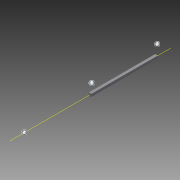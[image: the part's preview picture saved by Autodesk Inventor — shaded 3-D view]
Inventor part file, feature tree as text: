
AUTODESK INVENTOR PART (.ipt)
format: ipt  version: 2015 (Build 190159000, 159)  size: 156,672 bytes
history: native  units: in
note: dims shown in document units (in); Inventor stores cm internally (conversion verified against a paired STEP export)
features: other x5, extrude x1, imported_body x1, sketch x1
ambient origin geometry x8: Origin, YZ Plane, XZ Plane, XY Plane, X Axis, Y Axis, Z Axis, Center Point
bodies: Body1 (feature_tree)
feature tree (8):
  parser-record x1  (decoder bookkeeping rows leaked as tree rows — omitted from the tree; the rows remain in map.json)
  other  "Shaft"
  extrude  "length cut"  Depth=3.0in
  other  "front plane"
  imported_body  "Base1"
  sketch  "Sketch1"  dims[d1=0.0in d2=3.0in d3=0.0in d4=0.0in d5=0.0in]
  other  "main axis"
  other  "back plane"
